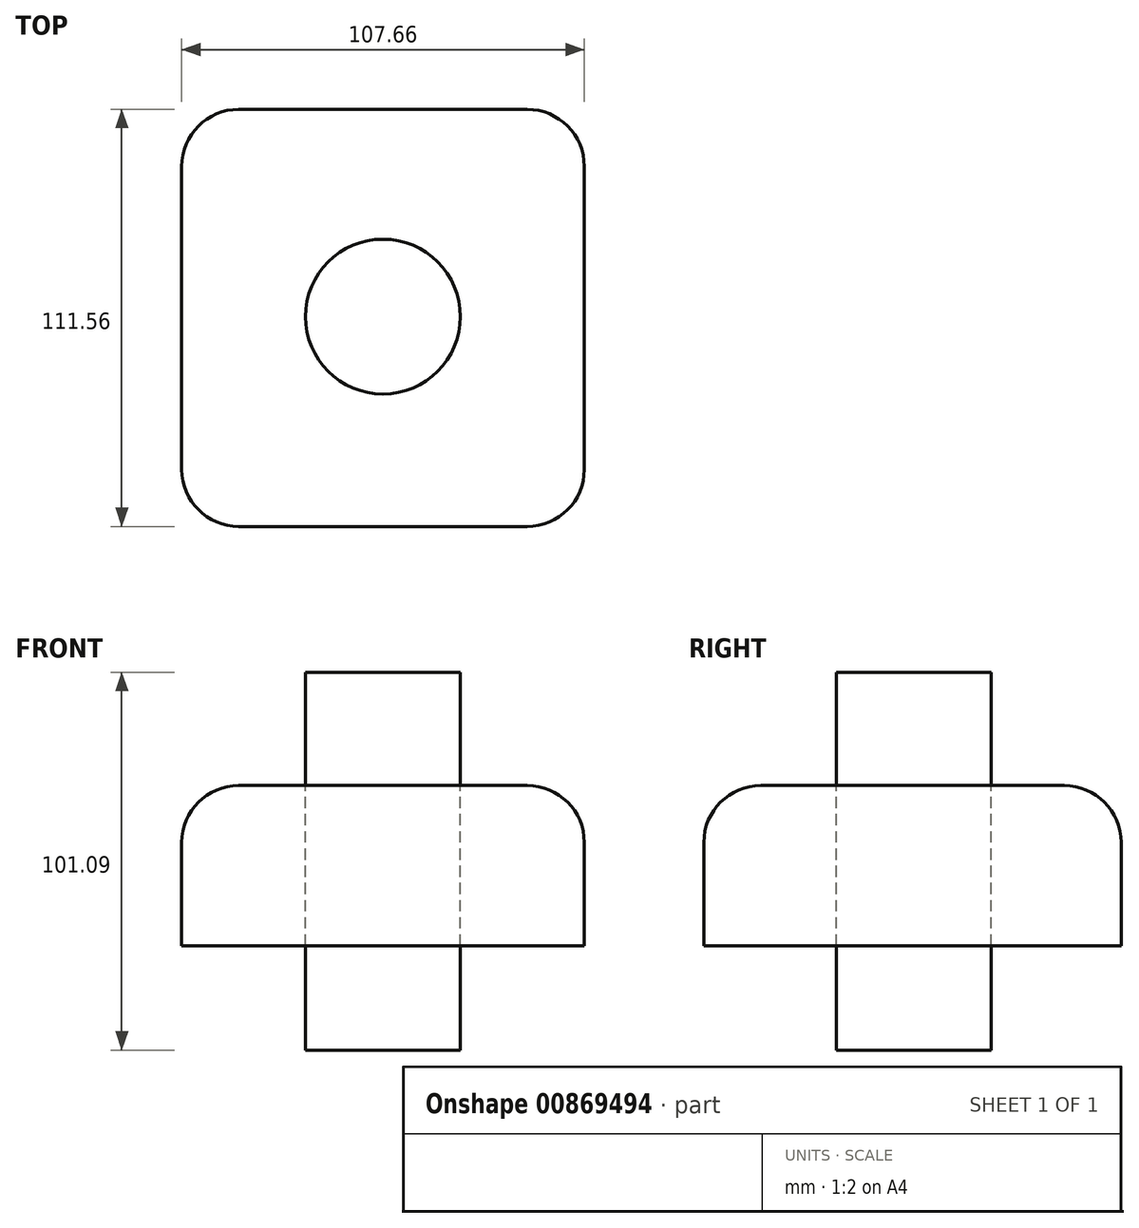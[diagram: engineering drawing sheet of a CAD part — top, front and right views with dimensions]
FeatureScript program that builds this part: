
annotation { "Feature Type Name" : "Feature", "Feature Type Description" : "" }
export const myFeature = defineFeature(function(context is Context, id is Id, definition is map)
    precondition{}
    {
        {
            var Q0;
            Q0=qCreatedBy(makeId("Top.planeOp"),FACE);
            var sketch = newSketch(context, id + "F0", { "sketchPlane" : qUnion([Q0])});
            skLineSegment(sketch, "E0.bottom", {"start": v(-52.85, 55.3) * mm, "end": v(54.8, 55.3) * mm});
            skLineSegment(sketch, "E0.top", {"start": v(-52.85, -56.27) * mm, "end": v(54.8, -56.27) * mm});
            skLineSegment(sketch, "E0.left", {"start": v(-52.85, 55.3) * mm, "end": v(-52.85, -56.27) * mm});
            skLineSegment(sketch, "E0.right", {"start": v(54.8, 55.3) * mm, "end": v(54.8, -56.27) * mm});
            skSolve(sketch);
        }
        {
            var Q0;
            Q0 = qSketchRegion(id + "F0", true);
            extrude(context, id + "F1", {"entities" : qUnion([Q0]), "depth" : 20 * mm, "offsetDistance" : 25.4 * mm});
        }
        {
            var Q0;
            Q0=makeQuery(id+"F1.opExtrude","SWEPT_EDGE",EDGE,{"disambiguationData":[OSD([sQuery(id+"F0.wireOp",EDGE,"E0.bottom"),sQuery(id+"F0.wireOp",EDGE,"E0.right")])]});
            var Q1;
            Q1=makeQuery(id+"F1.opExtrude","SWEPT_EDGE",EDGE,{"disambiguationData":[OSD([sQuery(id+"F0.wireOp",EDGE,"E0.top"),sQuery(id+"F0.wireOp",EDGE,"E0.right")])]});
            var Q2;
            Q2=makeQuery(id+"F1.opExtrude","SWEPT_EDGE",EDGE,{"disambiguationData":[OSD([sQuery(id+"F0.wireOp",EDGE,"E0.top"),sQuery(id+"F0.wireOp",EDGE,"E0.left")])]});
            var Q3;
            Q3=makeQuery(id+"F1.opExtrude","SWEPT_EDGE",EDGE,{"disambiguationData":[OSD([sQuery(id+"F0.wireOp",EDGE,"E0.bottom"),sQuery(id+"F0.wireOp",EDGE,"E0.left")])]});
            var Q4;
            Q4=makeQuery(id+"F1.opExtrude","CAP_FACE",FACE,{"disambiguationData":[OSD([sQuery(id+"F0.wireOp",EDGE,"E0.bottom"),sQuery(id+"F0.wireOp",EDGE,"E0.top"),sQuery(id+"F0.wireOp",EDGE,"E0.left"),sQuery(id+"F0.wireOp",EDGE,"E0.right")])],"isStart":false});
            fillet(context, id + "F2", {"entities" : qUnion([Q0, Q1, Q2, Q3, Q4]), "radius" : 15.24 * mm, "tangentPropagation" : true, "allowEdgeOverflow" : false});
        }
        {
            var Q0;
            Q0=qCreatedBy(makeId("Top.planeOp"),FACE);
            var sketch = newSketch(context, id + "F3", { "sketchPlane" : qUnion([Q0])});
            skCircle(sketch, "E1", {"center": v(7.3, 0) * mm, "radius": 20.5 * mm});
            skSolve(sketch);
        }
        {
            var Q0;
            Q0=makeQuery(id+"F3.imprint","IMPRINT",FACE,{"disambiguationData":[TD([[makeQuery(id+"F3.imprint","IMPRINT",EDGE,{"derivedFrom":sQuery(id+"F3.wireOp",EDGE,"E1")}),1.0]])]});
            var Q1;
            Q1=makeQuery(id+"F1.opExtrude","CAP_FACE",FACE,{"disambiguationData":[OSD([sQuery(id+"F0.wireOp",EDGE,"E0.bottom"),sQuery(id+"F0.wireOp",EDGE,"E0.top"),sQuery(id+"F0.wireOp",EDGE,"E0.left"),sQuery(id+"F0.wireOp",EDGE,"E0.right")])],"isStart":true});
            var Q2;
            Q2=makeQuery(id+"F1.opExtrude","CAP_FACE",FACE,{"disambiguationData":[OSD([sQuery(id+"F0.wireOp",EDGE,"E0.bottom"),sQuery(id+"F0.wireOp",EDGE,"E0.top"),sQuery(id+"F0.wireOp",EDGE,"E0.left"),sQuery(id+"F0.wireOp",EDGE,"E0.right")])],"isStart":false});
            extrude(context, id + "F4", {"entities" : qUnion([Q0, Q1, Q2]), "operationType" : NewBodyOperationType.ADD, "oppositeDirection" : true, "depth" : 22.86 * mm, "offsetDistance" : 25.4 * mm});
        }
        {
            var Q0;
            Q0=qCreatedBy(makeId("Top.planeOp"),FACE);
            var sketch = newSketch(context, id + "F5", { "sketchPlane" : qUnion([Q0])});
            skCircle(sketch, "E2", {"center": v(-106.48, 52.17) * mm, "radius": 20.72 * mm});
            skSolve(sketch);
        }
        {
            var Q0;
            Q0=makeQuery(id+"F5.imprint","IMPRINT",FACE,{"disambiguationData":[TD([[makeQuery(id+"F5.imprint","IMPRINT",EDGE,{"derivedFrom":sQuery(id+"F5.wireOp",EDGE,"E2")}),1.0]])]});
            extrude(context, id + "F6", {"entities" : qUnion([Q0]), "oppositeDirection" : true, "depth" : 101.1 * mm, "offsetDistance" : 25.4 * mm});
        }
        {
            var Q0;
            Q0=makeQuery(id+"F6.opExtrude","SWEPT_BODY",BODY,{"disambiguationData":[OSD([sQuery(id+"F5.wireOp",EDGE,"E2")])]});
            var Q1;
            Q1=makeQuery(id+"F6.opExtrude","CAP_FACE",FACE,{"disambiguationData":[OSD([sQuery(id+"F5.wireOp",EDGE,"E2")])],"isStart":true});
            transform(context, id + "F7", {"entities" : qUnion([Q0]), "transformType" : TransformType.TRANSLATION_3D, "dx" : 107.44 * mm, "dy" : -52.32 * mm, "dz" : 50.3 * mm, "makeCopy" : false});
        }
    });
